# Revit family: QF_BOURGEAT_Satellite4G_chaud_1-1_entree530_vitree_ouverture_droite
name_source: partatom
category: Equipement spécialisé
revit_build: Autodesk Revit 2015 (Build: 20140606_1530(x64)
units: mm (PartAtom-declared; Revit-internal decimal feet)

## types (6) — shared parameters
Certification = NF hygiene alimentaire
Diametre_roue = 160 mm  [stored 0.524934 ft]
Dimension_verticale_vitre = 704 mm  [stored 2.30971 ft]
Fabricant = BOURGEAT
Fréquence = 50 Hz
Hauteur_roue = 200 mm  [stored 0.656168 ft]
Indice de protection = IP25
Largeur_porte = 706 mm  [stored 2.31627 ft]
Longueur hors tout = 791 mm
Longueur_poignees_laterales = 648 mm  [stored 2.12598 ft]
Materiau_Poignee_porte = B_Elastomère_TPE_S
Materiau_bac = B_Elastomère_TPE_S
Materiau_bandage = B_Elastomère_TPE_S
Materiau_glissiere = Acrylique, transparent
Materiau_porte = Acier inoxydable, brossé
Materiau_vitre = Verre, vitrage transparent, trempé
Nature isolant = Mousse sans PU
Phase = 2
Pos_IHM_bord_gauche_porte_droite = 526 mm  [stored 1.72572 ft]
Pos_V_IHM = 98 mm  [stored 0.321522 ft]
Profondeur hors tout = 804 mm  [stored 2.6378 ft]
Spécification du Fabricant = Satellite 4G
Tension = 230 V
URL catalogue = http://www.bourgeat.fr

## per-type parameters (varying)
| type | Charge max | Consommation énergétique | Hauteur hors tout | Hauteur_poignee_porte_sol | Hauteur_poignees_laterales | Hauteur_porte | Humidification | Intensité nominale | Modèle | Poids net à vide | Pos_vitre_bord_gauche_porte_droite | Puissance électrique  |
| GN10_humidification_tirant_droit | 100.00 kg | 0.45 Kwh/h NFD40-016 | 1123 mm  [stored 3.68438 ft] | 372 mm  [stored 1.22047 ft] | 805 mm  [stored 2.64108 ft] | 876 mm  [stored 2.87402 ft] | Oui | 4 A | 841310 + 844000 | 80.00 kg | 103 mm  [stored 0.337927 ft] | 950 W |
| GN10_sans_humidification_tirant_droit | 100.00 kg | 0.45 Kwh/h NFD40-016 | 1123 mm  [stored 3.68438 ft] | 372 mm  [stored 1.22047 ft] | 805 mm  [stored 2.64108 ft] | 876 mm  [stored 2.87402 ft] | Non | 4 A | 841210 + 844000 | 80.00 kg | 102 mm | 950 W |
| GN15_sans_humidification_tirant_droit | 150.00 kg | 0.68 Kwh/h NFD40-016 | 1478 mm  [stored 4.84908 ft] | 512 mm  [stored 1.67979 ft] | 937 mm  [stored 3.07415 ft] | 1231 mm  [stored 4.03871 ft] | Non | 8 A | 841215 + 844000 | 120.00 kg | 102 mm | 1750 W |
| GN15_humidification_tirant_droit | 150.00 kg | 0.68 Kwh/h NFD40-016 | 1478 mm  [stored 4.84908 ft] | 512 mm  [stored 1.67979 ft] | 937 mm  [stored 3.07415 ft] | 1231 mm  [stored 4.03871 ft] | Oui | 8 A | 841315 + 844000 | 120.00 kg | 102 mm | 1750 W |
| GN20_humidification_tirant_droit | 200.00 kg | 0.88 Kwh/h NFD40-016 | 1833 mm  [stored 6.01378 ft] | 767 mm  [stored 2.5164 ft] | 937 mm  [stored 3.07415 ft] | 1586 mm  [stored 5.20341 ft] | Oui | 8 A | 841321 + 844000 | 140.00 kg | 102 mm | 1750 W |
| GN20_sans_humidification_tirant_droit | 200.00 kg | 0.88 Kwh/h NFD40-016 | 1833 mm  [stored 6.01378 ft] | 767 mm  [stored 2.5164 ft] | 937 mm  [stored 3.07415 ft] | 1586 mm  [stored 5.20341 ft] | Non | 8 A | 841221 + 844000 | 140.00 kg | 102 mm | 1750 W |

note: [stored X ft] marks values corroborated as IEEE doubles in the binary element streams (Revit-internal decimal feet)
